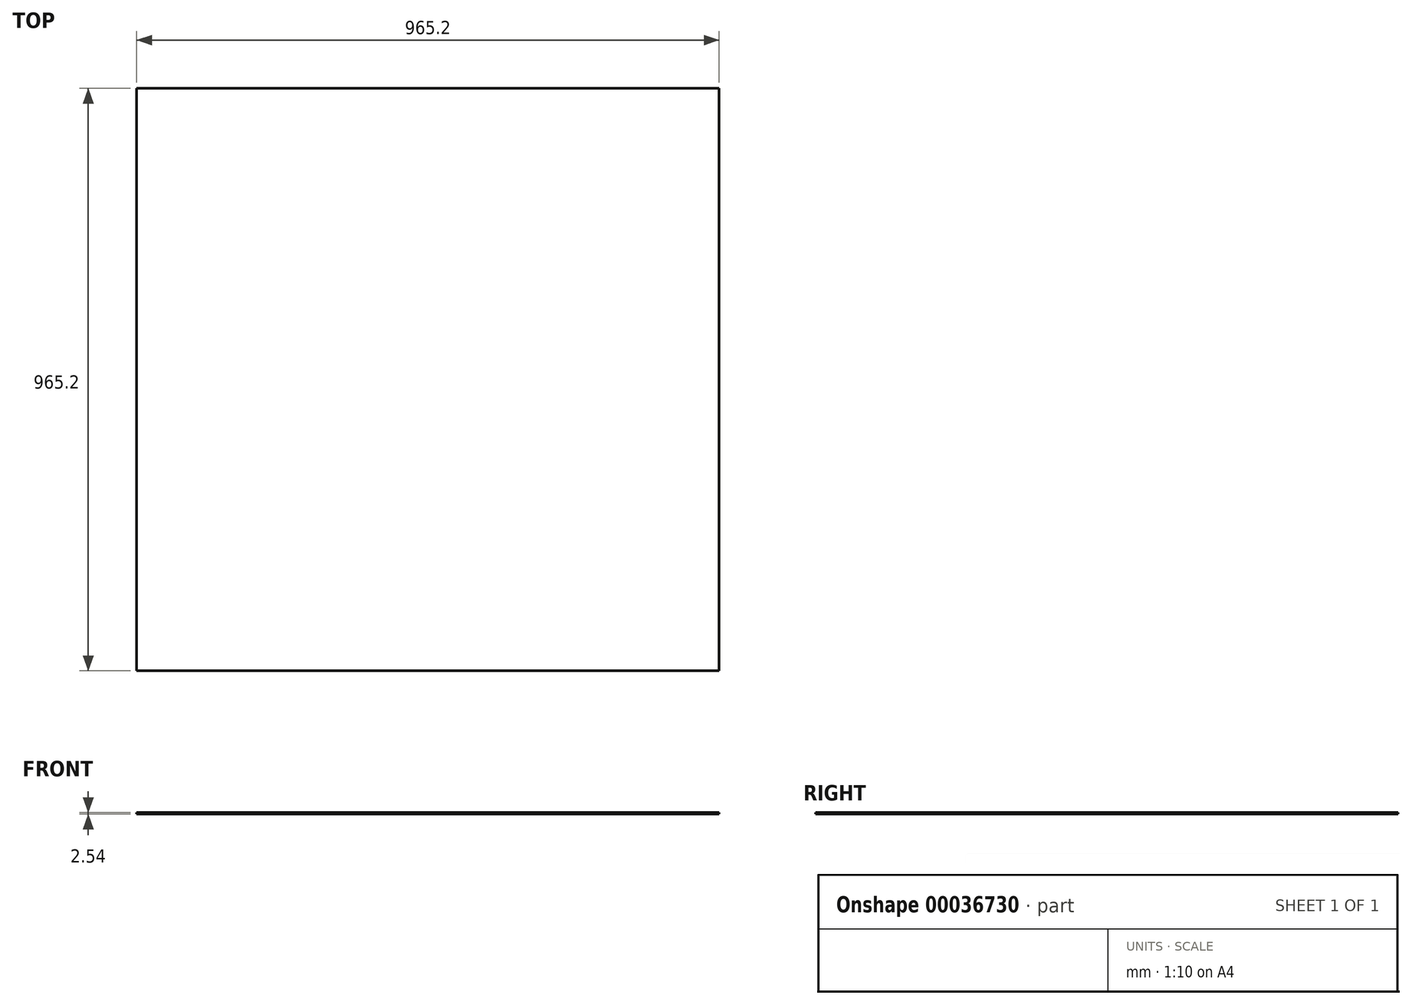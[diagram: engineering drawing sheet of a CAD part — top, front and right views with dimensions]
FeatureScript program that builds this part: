
annotation { "Feature Type Name" : "Feature", "Feature Type Description" : "" }
export const myFeature = defineFeature(function(context is Context, id is Id, definition is map)
    precondition{}
    {
        {
            var Q0;
            Q0=qCreatedBy(makeId("Top.planeOp"),FACE);
            var sketch = newSketch(context, id + "F0", { "sketchPlane" : qUnion([Q0])});
            skLineSegment(sketch, "E0.bottom", {"start": v(0, 0) * mm, "end": v(965.2, 0) * mm});
            skLineSegment(sketch, "E0.top", {"start": v(0, 965.2) * mm, "end": v(965.2, 965.2) * mm});
            skLineSegment(sketch, "E0.left", {"start": v(0, 0) * mm, "end": v(0, 965.2) * mm});
            skLineSegment(sketch, "E0.right", {"start": v(965.2, 0) * mm, "end": v(965.2, 965.2) * mm});
            skSolve(sketch);
        }
        {
            var Q0;
            Q0=makeQuery(id+"F0.imprint","IMPRINT",FACE,{"disambiguationData":[TD([[makeQuery(id+"F0.imprint","IMPRINT",EDGE,{"derivedFrom":sQuery(id+"F0.wireOp",EDGE,"E0.bottom")}),1.0]])]});
            extrude(context, id + "F1", {"entities" : qUnion([Q0]), "depth" : 2.54 * mm});
        }
    });
